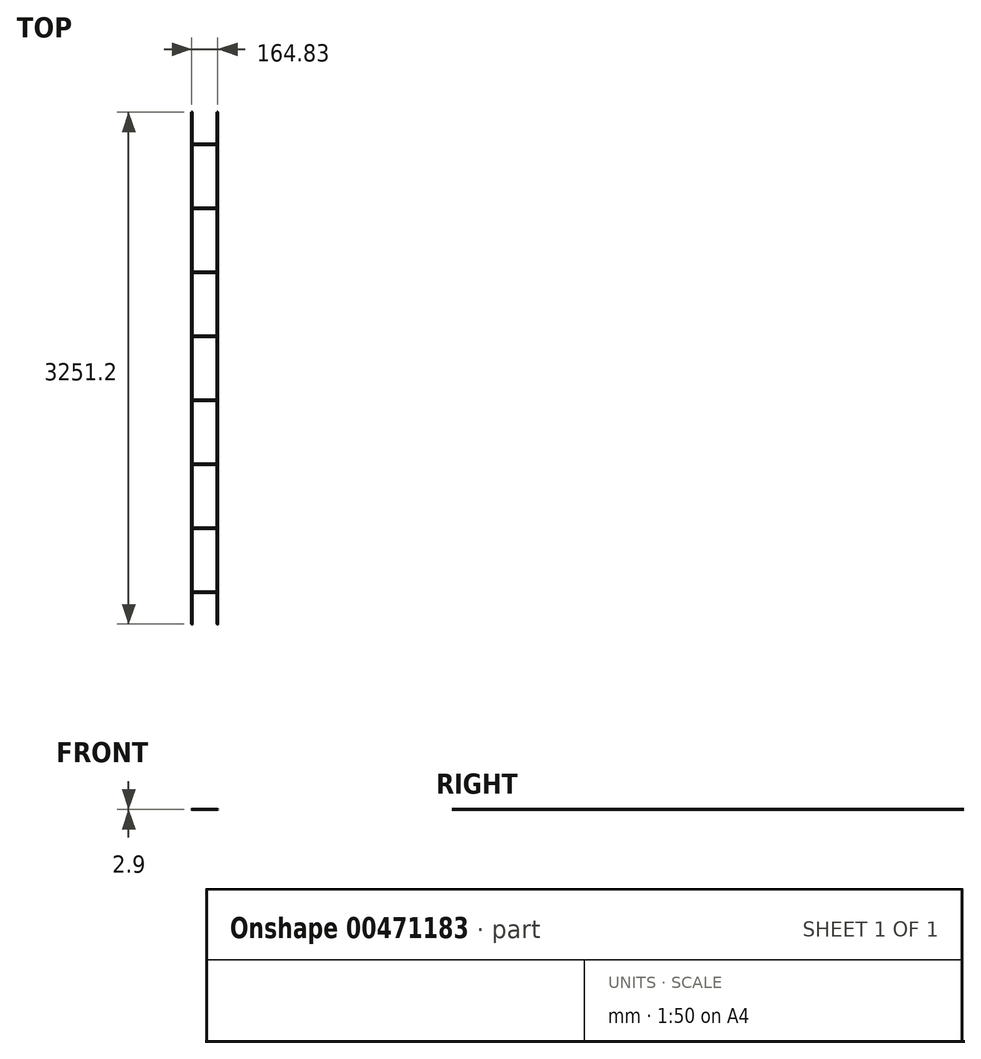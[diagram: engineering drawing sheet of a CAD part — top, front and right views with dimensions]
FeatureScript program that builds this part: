
annotation { "Feature Type Name" : "Feature", "Feature Type Description" : "" }
export const myFeature = defineFeature(function(context is Context, id is Id, definition is map)
    precondition{}
    {
        {
            var Q0;
            Q0=qCreatedBy(makeId("Front.planeOp"),FACE);
            var sketch = newSketch(context, id + "F0", { "sketchPlane" : qUnion([Q0])});
            skCircle(sketch, "E0", {"center": v(0, 0) * mm, "radius": 1.45 * mm});
            skSolve(sketch);
        }
        {
            var Q0;
            Q0=makeQuery(id+"F0.imprint","IMPRINT",FACE,{"disambiguationData":[TD([[makeQuery(id+"F0.imprint","IMPRINT",EDGE,{"derivedFrom":sQuery(id+"F0.wireOp",EDGE,"E0")}),1.0]])]});
            extrude(context, id + "F1", {"entities" : qUnion([Q0]), "depth" : 3251.2 * mm});
        }
        {
            var Q0;
            Q0=makeQuery(id+"F1.opExtrude","CAP_FACE",FACE,{"disambiguationData":[OSD([sQuery(id+"F0.wireOp",EDGE,"E0")])],"isStart":true});
            var sketch = newSketch(context, id + "F2", { "sketchPlane" : qUnion([Q0])});
            skLineSegment(sketch, "E1", {"start": v(0, 0) * mm, "end": v(161.93, 0) * mm});
            skCircle(sketch, "E2", {"center": v(161.93, 0) * mm, "radius": 1.45 * mm});
            skSolve(sketch);
        }
        {
            var Q0;
            Q0=makeQuery(id+"F2.imprint","IMPRINT",FACE,{"disambiguationData":[TD([[makeQuery(id+"F2.imprint","IMPRINT",EDGE,{"derivedFrom":sQuery(id+"F2.wireOp",EDGE,"E2")}),1.0]])]});
            extrude(context, id + "F3", {"entities" : qUnion([Q0]), "oppositeDirection" : true, "depth" : 3251.2 * mm});
        }
        {
            var Q0;
            Q0=qCreatedBy(makeId("Right.planeOp"),FACE);
            var sketch = newSketch(context, id + "F4", { "sketchPlane" : qUnion([Q0])});
            skLineSegment(sketch, "E3", {"start": v(0, 0) * mm, "end": v(-203.2, 0) * mm});
            skCircle(sketch, "E4", {"center": v(-203.2, 0) * mm, "radius": 1.45 * mm});
            skSolve(sketch);
        }
        {
            var Q0;
            Q0=makeQuery(id+"F4.imprint","IMPRINT",FACE,{"disambiguationData":[TD([[makeQuery(id+"F4.imprint","IMPRINT",EDGE,{"derivedFrom":sQuery(id+"F4.wireOp",EDGE,"E4")}),1.0]])]});
            extrude(context, id + "F5", {"entities" : qUnion([Q0]), "operationType" : NewBodyOperationType.ADD, "oppositeDirection" : true, "depth" : 161.92 * mm});
        }
        {
            var Q0;
            Q0=qCreatedBy(makeId("Right.planeOp"),FACE);
            var sketch = newSketch(context, id + "F6", { "sketchPlane" : qUnion([Q0])});
            skLineSegment(sketch, "E5", {"start": v(0, 0) * mm, "end": v(-203.2, 0) * mm});
            skLineSegment(sketch, "E6", {"start": v(-203.2, 0) * mm, "end": v(-609.6, 0) * mm});
            skLineSegment(sketch, "E7", {"start": v(-609.6, 0) * mm, "end": v(-1016, 0) * mm});
            skLineSegment(sketch, "E8", {"start": v(-1016, 0) * mm, "end": v(-1422.4, 0) * mm});
            skLineSegment(sketch, "E9", {"start": v(-1422.4, 0) * mm, "end": v(-1828.8, 0) * mm});
            skLineSegment(sketch, "E10", {"start": v(-1828.8, 0) * mm, "end": v(-2235.2, 0) * mm});
            skLineSegment(sketch, "E11", {"start": v(-2235.2, 0) * mm, "end": v(-2641.6, 0) * mm});
            skLineSegment(sketch, "E12", {"start": v(-2641.6, 0) * mm, "end": v(-3048, 0) * mm});
            skLineSegment(sketch, "E13", {"start": v(-3048, 0) * mm, "end": v(-3251.2, 0) * mm});
            skCircle(sketch, "E14", {"center": v(-609.6, 0) * mm, "radius": 1.45 * mm});
            skCircle(sketch, "E15", {"center": v(-1016, 0) * mm, "radius": 1.45 * mm});
            skCircle(sketch, "E16", {"center": v(-1422.4, 0) * mm, "radius": 1.45 * mm});
            skCircle(sketch, "E17", {"center": v(-1828.8, 0) * mm, "radius": 1.45 * mm});
            skCircle(sketch, "E18", {"center": v(-2235.2, 0) * mm, "radius": 1.45 * mm});
            skCircle(sketch, "E19", {"center": v(-2641.6, 0) * mm, "radius": 1.45 * mm});
            skCircle(sketch, "E20", {"center": v(-3048, 0) * mm, "radius": 1.45 * mm});
            skSolve(sketch);
        }
        {
            var Q0;
            {var subQ0=sQuery(id+"F6.wireOp",EDGE,"E7");var subQ1=sQuery(id+"F6.wireOp",EDGE,"E6");var subQ2=makeQuery(id+"F6.imprint","INTERSECT",VERTEX,{"derivedFrom":[subQ1,subQ0]});Q0=makeQuery(id+"F6.imprint","IMPRINT",FACE,{"disambiguationData":[TD([[makeQuery(id+"F6.imprint","IMPRINT",EDGE,{"disambiguationData":[TD([[subQ2,1.0]])],"derivedFrom":subQ1}),-1.0]])]});}
            var Q1;
            {var subQ0=sQuery(id+"F6.wireOp",EDGE,"E7");var subQ1=sQuery(id+"F6.wireOp",EDGE,"E6");var subQ2=makeQuery(id+"F6.imprint","INTERSECT",VERTEX,{"derivedFrom":[subQ1,subQ0]});Q1=makeQuery(id+"F6.imprint","IMPRINT",FACE,{"disambiguationData":[TD([[makeQuery(id+"F6.imprint","IMPRINT",EDGE,{"disambiguationData":[TD([[subQ2,1.0]])],"derivedFrom":subQ1}),1.0]])]});}
            var Q2;
            {var subQ0=sQuery(id+"F6.wireOp",EDGE,"E8");var subQ1=sQuery(id+"F6.wireOp",EDGE,"E7");var subQ2=makeQuery(id+"F6.imprint","INTERSECT",VERTEX,{"derivedFrom":[subQ1,subQ0]});Q2=makeQuery(id+"F6.imprint","IMPRINT",FACE,{"disambiguationData":[TD([[makeQuery(id+"F6.imprint","IMPRINT",EDGE,{"disambiguationData":[TD([[subQ2,1.0]])],"derivedFrom":subQ1}),-1.0]])]});}
            var Q3;
            {var subQ0=sQuery(id+"F6.wireOp",EDGE,"E8");var subQ1=sQuery(id+"F6.wireOp",EDGE,"E7");var subQ2=makeQuery(id+"F6.imprint","INTERSECT",VERTEX,{"derivedFrom":[subQ1,subQ0]});Q3=makeQuery(id+"F6.imprint","IMPRINT",FACE,{"disambiguationData":[TD([[makeQuery(id+"F6.imprint","IMPRINT",EDGE,{"disambiguationData":[TD([[subQ2,1.0]])],"derivedFrom":subQ1}),1.0]])]});}
            var Q4;
            {var subQ0=sQuery(id+"F6.wireOp",EDGE,"E9");var subQ1=sQuery(id+"F6.wireOp",EDGE,"E8");var subQ2=makeQuery(id+"F6.imprint","INTERSECT",VERTEX,{"derivedFrom":[subQ1,subQ0]});Q4=makeQuery(id+"F6.imprint","IMPRINT",FACE,{"disambiguationData":[TD([[makeQuery(id+"F6.imprint","IMPRINT",EDGE,{"disambiguationData":[TD([[subQ2,1.0]])],"derivedFrom":subQ1}),-1.0]])]});}
            var Q5;
            {var subQ0=sQuery(id+"F6.wireOp",EDGE,"E9");var subQ1=sQuery(id+"F6.wireOp",EDGE,"E8");var subQ2=makeQuery(id+"F6.imprint","INTERSECT",VERTEX,{"derivedFrom":[subQ1,subQ0]});Q5=makeQuery(id+"F6.imprint","IMPRINT",FACE,{"disambiguationData":[TD([[makeQuery(id+"F6.imprint","IMPRINT",EDGE,{"disambiguationData":[TD([[subQ2,1.0]])],"derivedFrom":subQ1}),1.0]])]});}
            var Q6;
            {var subQ0=sQuery(id+"F6.wireOp",EDGE,"E10");var subQ1=sQuery(id+"F6.wireOp",EDGE,"E9");var subQ2=makeQuery(id+"F6.imprint","INTERSECT",VERTEX,{"derivedFrom":[subQ1,subQ0]});Q6=makeQuery(id+"F6.imprint","IMPRINT",FACE,{"disambiguationData":[TD([[makeQuery(id+"F6.imprint","IMPRINT",EDGE,{"disambiguationData":[TD([[subQ2,1.0]])],"derivedFrom":subQ1}),-1.0]])]});}
            var Q7;
            {var subQ0=sQuery(id+"F6.wireOp",EDGE,"E10");var subQ1=sQuery(id+"F6.wireOp",EDGE,"E9");var subQ2=makeQuery(id+"F6.imprint","INTERSECT",VERTEX,{"derivedFrom":[subQ1,subQ0]});Q7=makeQuery(id+"F6.imprint","IMPRINT",FACE,{"disambiguationData":[TD([[makeQuery(id+"F6.imprint","IMPRINT",EDGE,{"disambiguationData":[TD([[subQ2,1.0]])],"derivedFrom":subQ1}),1.0]])]});}
            var Q8;
            {var subQ0=sQuery(id+"F6.wireOp",EDGE,"E11");var subQ1=sQuery(id+"F6.wireOp",EDGE,"E10");var subQ2=makeQuery(id+"F6.imprint","INTERSECT",VERTEX,{"derivedFrom":[subQ1,subQ0]});Q8=makeQuery(id+"F6.imprint","IMPRINT",FACE,{"disambiguationData":[TD([[makeQuery(id+"F6.imprint","IMPRINT",EDGE,{"disambiguationData":[TD([[subQ2,1.0]])],"derivedFrom":subQ1}),-1.0]])]});}
            var Q9;
            {var subQ0=sQuery(id+"F6.wireOp",EDGE,"E11");var subQ1=sQuery(id+"F6.wireOp",EDGE,"E10");var subQ2=makeQuery(id+"F6.imprint","INTERSECT",VERTEX,{"derivedFrom":[subQ1,subQ0]});Q9=makeQuery(id+"F6.imprint","IMPRINT",FACE,{"disambiguationData":[TD([[makeQuery(id+"F6.imprint","IMPRINT",EDGE,{"disambiguationData":[TD([[subQ2,1.0]])],"derivedFrom":subQ1}),1.0]])]});}
            var Q10;
            {var subQ0=sQuery(id+"F6.wireOp",EDGE,"E12");var subQ1=sQuery(id+"F6.wireOp",EDGE,"E11");var subQ2=makeQuery(id+"F6.imprint","INTERSECT",VERTEX,{"derivedFrom":[subQ1,subQ0]});Q10=makeQuery(id+"F6.imprint","IMPRINT",FACE,{"disambiguationData":[TD([[makeQuery(id+"F6.imprint","IMPRINT",EDGE,{"disambiguationData":[TD([[subQ2,1.0]])],"derivedFrom":subQ1}),-1.0]])]});}
            var Q11;
            {var subQ0=sQuery(id+"F6.wireOp",EDGE,"E12");var subQ1=sQuery(id+"F6.wireOp",EDGE,"E11");var subQ2=makeQuery(id+"F6.imprint","INTERSECT",VERTEX,{"derivedFrom":[subQ1,subQ0]});Q11=makeQuery(id+"F6.imprint","IMPRINT",FACE,{"disambiguationData":[TD([[makeQuery(id+"F6.imprint","IMPRINT",EDGE,{"disambiguationData":[TD([[subQ2,1.0]])],"derivedFrom":subQ1}),1.0]])]});}
            var Q12;
            {var subQ0=sQuery(id+"F6.wireOp",EDGE,"E13");var subQ1=sQuery(id+"F6.wireOp",EDGE,"E12");var subQ2=makeQuery(id+"F6.imprint","INTERSECT",VERTEX,{"derivedFrom":[subQ1,subQ0]});Q12=makeQuery(id+"F6.imprint","IMPRINT",FACE,{"disambiguationData":[TD([[makeQuery(id+"F6.imprint","IMPRINT",EDGE,{"disambiguationData":[TD([[subQ2,1.0]])],"derivedFrom":subQ1}),-1.0]])]});}
            var Q13;
            {var subQ0=sQuery(id+"F6.wireOp",EDGE,"E13");var subQ1=sQuery(id+"F6.wireOp",EDGE,"E12");var subQ2=makeQuery(id+"F6.imprint","INTERSECT",VERTEX,{"derivedFrom":[subQ1,subQ0]});Q13=makeQuery(id+"F6.imprint","IMPRINT",FACE,{"disambiguationData":[TD([[makeQuery(id+"F6.imprint","IMPRINT",EDGE,{"disambiguationData":[TD([[subQ2,1.0]])],"derivedFrom":subQ1}),1.0]])]});}
            extrude(context, id + "F7", {"entities" : qUnion([Q0, Q1, Q2, Q3, Q4, Q5, Q6, Q7, Q8, Q9, Q10, Q11, Q12, Q13]), "oppositeDirection" : true, "depth" : 161.92 * mm});
        }
    });
